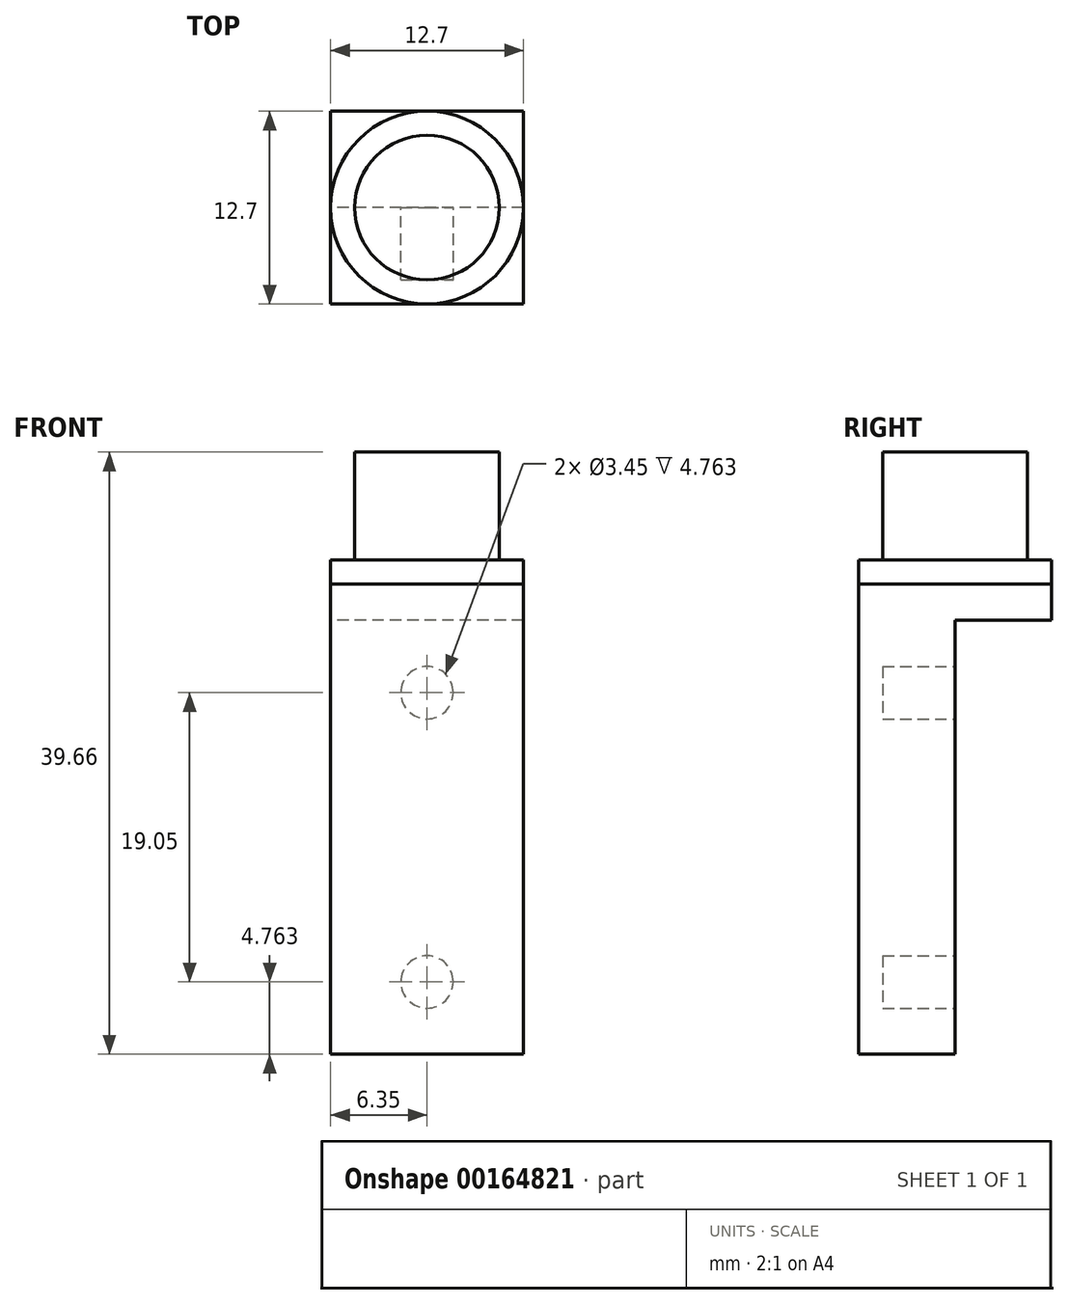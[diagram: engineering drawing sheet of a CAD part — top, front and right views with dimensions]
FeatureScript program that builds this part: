
annotation { "Feature Type Name" : "Feature", "Feature Type Description" : "" }
export const myFeature = defineFeature(function(context is Context, id is Id, definition is map)
    precondition{}
    {
        {
            var Q0;
            Q0=qCreatedBy(makeId("Top.planeOp"),FACE);
            var sketch = newSketch(context, id + "F0", { "sketchPlane" : qUnion([Q0])});
            skLineSegment(sketch, "E0.bottom", {"start": v(6.35, -6.35) * mm, "end": v(-6.35, -6.35) * mm});
            skLineSegment(sketch, "E0.top", {"start": v(6.35, 6.35) * mm, "end": v(-6.35, 6.35) * mm});
            skLineSegment(sketch, "E0.left", {"start": v(6.35, -6.35) * mm, "end": v(6.35, 6.35) * mm});
            skLineSegment(sketch, "E0.right", {"start": v(-6.35, -6.35) * mm, "end": v(-6.35, 6.35) * mm});
            skPoint(sketch, "E0.middle", {"position": v(0, 0) * mm});
            skSolve(sketch);
        }
        {
            var Q0;
            Q0 = qSketchRegion(id + "F0", true);
            extrude(context, id + "F1", {"entities" : qUnion([Q0]), "depth" : 30.96 * mm});
        }
        {
            var Q0;
            Q0=makeQuery(id+"F1.opExtrude","CAP_FACE",FACE,{"disambiguationData":[OSD([sQuery(id+"F0.wireOp",EDGE,"E0.bottom"),sQuery(id+"F0.wireOp",EDGE,"E0.top"),sQuery(id+"F0.wireOp",EDGE,"E0.left"),sQuery(id+"F0.wireOp",EDGE,"E0.right")])],"isStart":false});
            var sketch = newSketch(context, id + "F2", { "sketchPlane" : qUnion([Q0])});
            skCircle(sketch, "E1", {"center": v(0, 0) * mm, "radius": 6.35 * mm});
            skSolve(sketch);
        }
        {
            var Q0;
            Q0 = qSketchRegion(id + "F2", true);
            extrude(context, id + "F3", {"entities" : qUnion([Q0]), "operationType" : NewBodyOperationType.ADD, "depth" : 1.59 * mm});
        }
        {
            var Q0;
            Q0=makeQuery(id+"F3.opExtrude","CAP_FACE",FACE,{"disambiguationData":[OSD([sQuery(id+"F2.wireOp",EDGE,"E1")])],"isStart":false});
            var sketch = newSketch(context, id + "F4", { "sketchPlane" : qUnion([Q0])});
            skCircle(sketch, "E2", {"center": v(0, 0) * mm, "radius": 4.76 * mm});
            skSolve(sketch);
        }
        {
            var Q0;
            Q0 = qSketchRegion(id + "F4", true);
            extrude(context, id + "F5", {"entities" : qUnion([Q0]), "operationType" : NewBodyOperationType.ADD, "depth" : 7.11 * mm});
        }
        {
            var Q0;
            Q0=makeQuery(id+"F1.opExtrude","SWEPT_FACE",FACE,{"disambiguationData":[OSD([sQuery(id+"F0.wireOp",EDGE,"E0.right")])]});
            var sketch = newSketch(context, id + "F6", { "sketchPlane" : qUnion([Q0])});
            skLineSegment(sketch, "E3.bottom", {"start": v(-6.35, 28.58) * mm, "end": v(0, 28.58) * mm});
            skLineSegment(sketch, "E3.top", {"start": v(-6.35, 0) * mm, "end": v(0, 0) * mm});
            skLineSegment(sketch, "E3.left", {"start": v(-6.35, 28.58) * mm, "end": v(-6.35, 0) * mm});
            skLineSegment(sketch, "E3.right", {"start": v(0, 28.58) * mm, "end": v(0, 0) * mm});
            skSolve(sketch);
        }
        {
            var Q0;
            Q0 = qSketchRegion(id + "F6", true);
            var Q1;
            Q1=makeQuery(id+"F1.opExtrude","SWEPT_FACE",FACE,{"disambiguationData":[OSD([sQuery(id+"F0.wireOp",EDGE,"E0.left")])]});
            extrude(context, id + "F7", {"entities" : qUnion([Q0]), "operationType" : NewBodyOperationType.REMOVE, "endBound" : BoundingType.UP_TO_SURFACE, "oppositeDirection" : true, "endBoundEntityFace" : qUnion([Q1]), "depth" : 25.4 * mm});
        }
        {
            var Q0;
            Q0=makeQuery(id+"F7.boolean.opBoolean","COPY",FACE,{"derivedFrom":makeQuery(id+"F7.opExtrude","SWEPT_FACE",FACE,{"disambiguationData":[OSD([sQuery(id+"F6.wireOp",EDGE,"E3.right")])]})});
            var sketch = newSketch(context, id + "F8", { "sketchPlane" : qUnion([Q0])});
            skLineSegment(sketch, "E4", {"start": v(0, 28.58) * mm, "end": v(0, 23.81) * mm, "construction": true});
            skLineSegment(sketch, "E5", {"start": v(0, 0) * mm, "end": v(0, 4.76) * mm, "construction": true});
            skCircle(sketch, "E6", {"center": v(0, 23.81) * mm, "radius": 1.73 * mm});
            skCircle(sketch, "E7", {"center": v(0, 4.76) * mm, "radius": 1.73 * mm});
            skSolve(sketch);
        }
        {
            var Q0;
            Q0 = qSketchRegion(id + "F8", true);
            extrude(context, id + "F9", {"entities" : qUnion([Q0]), "operationType" : NewBodyOperationType.REMOVE, "oppositeDirection" : true, "depth" : 4.76 * mm});
        }
    });
